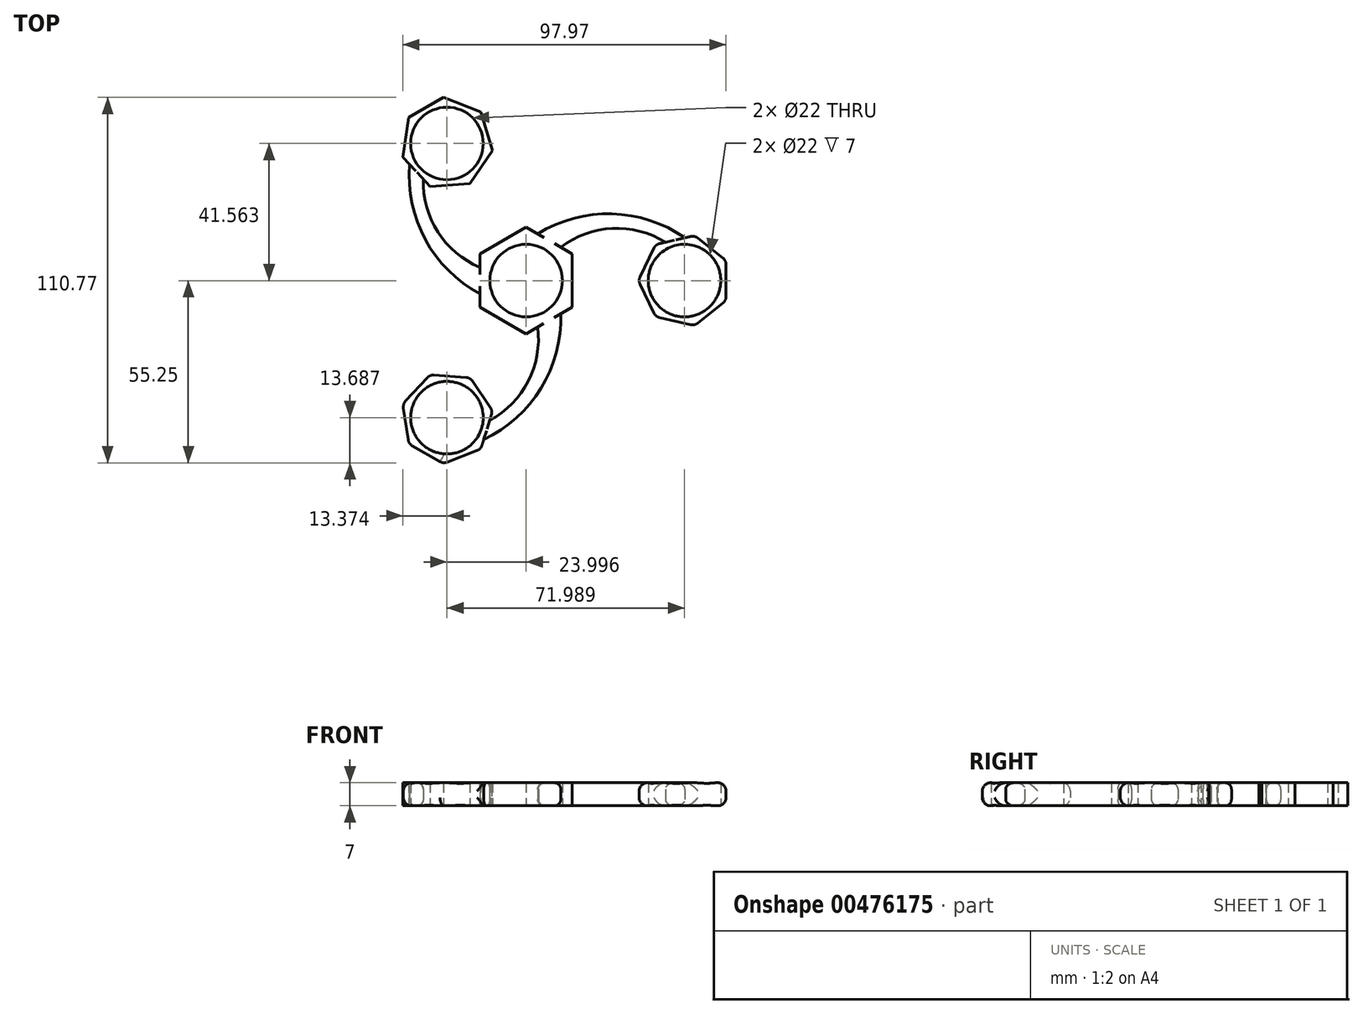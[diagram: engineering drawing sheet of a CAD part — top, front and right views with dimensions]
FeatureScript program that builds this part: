
annotation { "Feature Type Name" : "Feature", "Feature Type Description" : "" }
export const myFeature = defineFeature(function(context is Context, id is Id, definition is map)
    precondition{}
    {
        {
            var Q0;
            Q0=qCreatedBy(makeId("Top.planeOp"),FACE);
            var sketch = newSketch(context, id + "F0", { "sketchPlane" : qUnion([Q0])});
            skCircle(sketch, "E0", {"center": v(0, 0) * mm, "radius": 11 * mm});
            skCircle(sketch, "E1", {"center": v(48, 0) * mm, "radius": 11 * mm});
            skArc(sketch, "E2.cCircle", {"start": v(36.63, 5.47) * mm, "mid": v(50.8, -12.3) * mm, "end": v(55.85, 9.86) * mm, "construction": true});
            skLineSegment(sketch, "E2.0", {"start": v(60.6, 6.07) * mm, "end": v(60.6, -6.07) * mm});
            skLineSegment(sketch, "E2.1", {"start": v(60.6, -6.07) * mm, "end": v(51.1, -13.64) * mm});
            skLineSegment(sketch, "E2.2", {"start": v(51.1, -13.64) * mm, "end": v(39.27, -10.94) * mm});
            skLineSegment(sketch, "E2.3", {"start": v(39.27, -10.94) * mm, "end": v(34, 0) * mm});
            skLineSegment(sketch, "E2.4", {"start": v(34, 0) * mm, "end": v(39.27, 10.94) * mm});
            skLineSegment(sketch, "E2.5", {"start": v(39.27, 10.94) * mm, "end": v(42.23, 11.62) * mm});
            skLineSegment(sketch, "E2.6", {"start": v(51.1, 13.64) * mm, "end": v(60.6, 6.07) * mm});
            skPoint(sketch, "E2.0.midPoint", {"position": v(60.6, 0) * mm});
            skLineSegment(sketch, "E3.0", {"start": v(14, 8.08) * mm, "end": v(14, -8.08) * mm});
            skLineSegment(sketch, "E3.1", {"start": v(14, -8.08) * mm, "end": v(10.5, -10.1) * mm});
            skLineSegment(sketch, "E3.2", {"start": v(0, -16.17) * mm, "end": v(-14, -8.08) * mm});
            skLineSegment(sketch, "E3.3", {"start": v(-14, -8.08) * mm, "end": v(-14, -4.04) * mm});
            skLineSegment(sketch, "E3.4", {"start": v(-14, 8.08) * mm, "end": v(0, 16.17) * mm});
            skLineSegment(sketch, "E3.5", {"start": v(0, 16.17) * mm, "end": v(3.5, 14.15) * mm});
            skPoint(sketch, "E3.0.midPoint", {"position": v(14, 0) * mm});
            skLineSegment(sketch, "E4", {"start": v(14, -8.08) * mm, "end": v(14, 0) * mm});
            skLineSegment(sketch, "E5", {"start": v(14, 0) * mm, "end": v(14, 8.08) * mm});
            skLineSegment(sketch, "E6", {"start": v(14, 8.08) * mm, "end": v(10.5, 10.1) * mm});
            skLineSegment(sketch, "E7", {"start": v(10.5, 10.1) * mm, "end": v(14, 8.08) * mm});
            skLineSegment(sketch, "E8", {"start": v(3.5, 14.15) * mm, "end": v(0, 16.17) * mm});
            skLineSegment(sketch, "E9", {"start": v(48.15, 12.97) * mm, "end": v(51.1, 13.64) * mm});
            skLineSegment(sketch, "E10", {"start": v(42.23, 11.62) * mm, "end": v(39.27, 10.94) * mm});
            skArc(sketch, "E11", {"start": v(42.23, 11.62) * mm, "mid": v(26.13, 15.8) * mm, "end": v(10.5, 10.1) * mm});
            skArc(sketch, "E12", {"start": v(48.15, 12.97) * mm, "mid": v(26, 20.24) * mm, "end": v(3.5, 14.15) * mm});
            skArc(sketch, "E13.1.0", {"start": v(-35.3, 35.21) * mm, "mid": v(-30.53, 12.4) * mm, "end": v(-14, -4.04) * mm});
            skArc(sketch, "E13.1.1", {"start": v(-31.17, 30.76) * mm, "mid": v(-26.75, 14.73) * mm, "end": v(-14, 4.04) * mm});
            skLineSegment(sketch, "E13.1.2", {"start": v(-17, 29.44) * mm, "end": v(-29.1, 28.54) * mm});
            skLineSegment(sketch, "E13.1.3", {"start": v(-10.16, 39.48) * mm, "end": v(-17, 29.44) * mm});
            skLineSegment(sketch, "E13.1.4", {"start": v(-13.74, 51.08) * mm, "end": v(-10.16, 39.48) * mm});
            skLineSegment(sketch, "E13.1.5", {"start": v(-25.04, 55.52) * mm, "end": v(-13.74, 51.08) * mm});
            skLineSegment(sketch, "E13.1.6", {"start": v(-35.56, 49.44) * mm, "end": v(-25.04, 55.52) * mm});
            skLineSegment(sketch, "E13.1.7", {"start": v(-37.37, 37.44) * mm, "end": v(-35.56, 49.44) * mm});
            skLineSegment(sketch, "E13.1.8", {"start": v(-35.3, 35.21) * mm, "end": v(-37.37, 37.44) * mm});
            skLineSegment(sketch, "E13.1.9", {"start": v(-29.1, 28.54) * mm, "end": v(-31.17, 30.76) * mm});
            skCircle(sketch, "E13.1.10", {"center": v(-24, 41.56) * mm, "radius": 11 * mm});
            skArc(sketch, "E13.2.0", {"start": v(-12.84, -48.18) * mm, "mid": v(4.53, -32.64) * mm, "end": v(10.5, -10.1) * mm});
            skArc(sketch, "E13.2.1", {"start": v(-11.05, -42.38) * mm, "mid": v(0.62, -30.53) * mm, "end": v(3.5, -14.15) * mm});
            skLineSegment(sketch, "E13.2.2", {"start": v(-17, -29.44) * mm, "end": v(-10.16, -39.48) * mm});
            skLineSegment(sketch, "E13.2.3", {"start": v(-29.1, -28.54) * mm, "end": v(-17, -29.44) * mm});
            skLineSegment(sketch, "E13.2.4", {"start": v(-37.37, -37.44) * mm, "end": v(-29.1, -28.54) * mm});
            skLineSegment(sketch, "E13.2.5", {"start": v(-35.56, -49.44) * mm, "end": v(-37.37, -37.44) * mm});
            skLineSegment(sketch, "E13.2.6", {"start": v(-25.04, -55.52) * mm, "end": v(-35.56, -49.44) * mm});
            skLineSegment(sketch, "E13.2.7", {"start": v(-13.74, -51.08) * mm, "end": v(-25.04, -55.52) * mm});
            skLineSegment(sketch, "E13.2.8", {"start": v(-12.84, -48.18) * mm, "end": v(-13.74, -51.08) * mm});
            skLineSegment(sketch, "E13.2.9", {"start": v(-10.16, -39.48) * mm, "end": v(-11.05, -42.38) * mm});
            skCircle(sketch, "E13.2.10", {"center": v(-24, -41.56) * mm, "radius": 11 * mm});
            skLineSegment(sketch, "E14.trimOffspring", {"start": v(3.5, -14.15) * mm, "end": v(0, -16.17) * mm});
            skLineSegment(sketch, "E15.trimOffspring", {"start": v(-14, 4.04) * mm, "end": v(-14, 8.08) * mm});
            skSolve(sketch);
        }
        {
            var Q0;
            Q0=makeQuery(id+"F0.imprint","IMPRINT",FACE,{"disambiguationData":[TD([[makeQuery(id+"F0.imprint","IMPRINT",EDGE,{"derivedFrom":sQuery(id+"F0.wireOp",EDGE,"E0")}),-1.0]])]});
            extrude(context, id + "F1", {"entities" : qUnion([Q0]), "depth" : 7 * mm});
        }
        {
            var Q0;
            Q0=makeQuery(id+"F1.opExtrude","CAP_EDGE",EDGE,{"disambiguationData":[OSD([sQuery(id+"F0.wireOp",EDGE,"E13.1.0")])],"isStart":false});
            var Q1;
            Q1=makeQuery(id+"F1.opExtrude","CAP_EDGE",EDGE,{"disambiguationData":[OSD([sQuery(id+"F0.wireOp",EDGE,"E13.2.0")])],"isStart":false});
            var Q2;
            Q2=makeQuery(id+"F1.opExtrude","CAP_EDGE",EDGE,{"disambiguationData":[OSD([sQuery(id+"F0.wireOp",EDGE,"E13.2.1")])],"isStart":false});
            var Q3;
            Q3=makeQuery(id+"F1.opExtrude","CAP_EDGE",EDGE,{"disambiguationData":[OSD([sQuery(id+"F0.wireOp",EDGE,"E11")])],"isStart":false});
            var Q4;
            Q4=makeQuery(id+"F1.opExtrude","CAP_EDGE",EDGE,{"disambiguationData":[OSD([sQuery(id+"F0.wireOp",EDGE,"E12")])],"isStart":false});
            var Q5;
            Q5=makeQuery(id+"F1.opExtrude","CAP_EDGE",EDGE,{"disambiguationData":[OSD([sQuery(id+"F0.wireOp",EDGE,"E13.1.1")])],"isStart":false});
            var Q6;
            Q6=makeQuery(id+"F1.opExtrude","CAP_EDGE",EDGE,{"disambiguationData":[OSD([sQuery(id+"F0.wireOp",EDGE,"E13.2.0")])],"isStart":true});
            var Q7;
            Q7=makeQuery(id+"F1.opExtrude","CAP_EDGE",EDGE,{"disambiguationData":[OSD([sQuery(id+"F0.wireOp",EDGE,"E13.2.1")])],"isStart":true});
            var Q8;
            Q8=makeQuery(id+"F1.opExtrude","CAP_EDGE",EDGE,{"disambiguationData":[OSD([sQuery(id+"F0.wireOp",EDGE,"E11")])],"isStart":true});
            var Q9;
            Q9=makeQuery(id+"F1.opExtrude","CAP_EDGE",EDGE,{"disambiguationData":[OSD([sQuery(id+"F0.wireOp",EDGE,"E12")])],"isStart":true});
            var Q10;
            Q10=makeQuery(id+"F1.opExtrude","CAP_EDGE",EDGE,{"disambiguationData":[OSD([sQuery(id+"F0.wireOp",EDGE,"E13.1.1")])],"isStart":true});
            var Q11;
            Q11=makeQuery(id+"F1.opExtrude","CAP_EDGE",EDGE,{"disambiguationData":[OSD([sQuery(id+"F0.wireOp",EDGE,"E13.1.0")])],"isStart":true});
            fillet(context, id + "F2", {"entities" : qUnion([Q0, Q1, Q2, Q3, Q4, Q5, Q6, Q7, Q8, Q9, Q10, Q11]), "radius" : 2 * mm, "tangentPropagation" : true, "allowEdgeOverflow" : false});
        }
        {
            var Q0;
            Q0=makeQuery(id+"F1.opExtrude","CAP_EDGE",EDGE,{"disambiguationData":[OSD([sQuery(id+"F0.wireOp",EDGE,"E13.2.4")])],"isStart":true});
            var Q1;
            Q1=makeQuery(id+"F1.opExtrude","CAP_EDGE",EDGE,{"disambiguationData":[OSD([sQuery(id+"F0.wireOp",EDGE,"E13.2.5")])],"isStart":true});
            var Q2;
            Q2=makeQuery(id+"F1.opExtrude","CAP_EDGE",EDGE,{"disambiguationData":[OSD([sQuery(id+"F0.wireOp",EDGE,"E13.2.6")])],"isStart":true});
            var Q3;
            Q3=makeQuery(id+"F1.opExtrude","CAP_EDGE",EDGE,{"disambiguationData":[OSD([sQuery(id+"F0.wireOp",EDGE,"E13.2.3")])],"isStart":true});
            var Q4;
            Q4=makeQuery(id+"F1.opExtrude","CAP_EDGE",EDGE,{"disambiguationData":[OSD([sQuery(id+"F0.wireOp",EDGE,"E13.2.2")])],"isStart":true});
            var Q5;
            Q5=makeQuery(id+"F1.opExtrude","CAP_EDGE",EDGE,{"disambiguationData":[OSD([sQuery(id+"F0.wireOp",EDGE,"E13.2.7")])],"isStart":true});
            var Q6;
            Q6=makeQuery(id+"F1.opExtrude","CAP_EDGE",EDGE,{"disambiguationData":[OSD([sQuery(id+"F0.wireOp",EDGE,"E13.2.6")])],"isStart":false});
            var Q7;
            Q7=makeQuery(id+"F1.opExtrude","CAP_EDGE",EDGE,{"disambiguationData":[OSD([sQuery(id+"F0.wireOp",EDGE,"E13.2.7")])],"isStart":false});
            var Q8;
            Q8=makeQuery(id+"F1.opExtrude","CAP_EDGE",EDGE,{"disambiguationData":[OSD([sQuery(id+"F0.wireOp",EDGE,"E13.2.2")])],"isStart":false});
            var Q9;
            Q9=makeQuery(id+"F1.opExtrude","CAP_EDGE",EDGE,{"disambiguationData":[OSD([sQuery(id+"F0.wireOp",EDGE,"E13.2.3")])],"isStart":false});
            var Q10;
            Q10=makeQuery(id+"F1.opExtrude","CAP_EDGE",EDGE,{"disambiguationData":[OSD([sQuery(id+"F0.wireOp",EDGE,"E13.2.4")])],"isStart":false});
            var Q11;
            Q11=makeQuery(id+"F1.opExtrude","CAP_EDGE",EDGE,{"disambiguationData":[OSD([sQuery(id+"F0.wireOp",EDGE,"E13.2.5")])],"isStart":false});
            var Q12;
            Q12=makeQuery(id+"F1.opExtrude","SWEPT_EDGE",EDGE,{"disambiguationData":[OSD([sQuery(id+"F0.wireOp",EDGE,"E13.2.4"),sQuery(id+"F0.wireOp",EDGE,"E13.2.5")])]});
            var Q13;
            Q13=makeQuery(id+"F1.opExtrude","SWEPT_EDGE",EDGE,{"disambiguationData":[OSD([sQuery(id+"F0.wireOp",EDGE,"E13.2.5"),sQuery(id+"F0.wireOp",EDGE,"E13.2.6")])]});
            var Q14;
            Q14=makeQuery(id+"F1.opExtrude","SWEPT_EDGE",EDGE,{"disambiguationData":[OSD([sQuery(id+"F0.wireOp",EDGE,"E13.2.6"),sQuery(id+"F0.wireOp",EDGE,"E13.2.7")])]});
            var Q15;
            Q15=makeQuery(id+"F1.opExtrude","SWEPT_FACE",FACE,{"disambiguationData":[OSD([sQuery(id+"F0.wireOp",EDGE,"E13.2.4")])]});
            var Q16;
            Q16=makeQuery(id+"F1.opExtrude","SWEPT_FACE",FACE,{"disambiguationData":[OSD([sQuery(id+"F0.wireOp",EDGE,"E13.2.3")])]});
            var Q17;
            Q17=makeQuery(id+"F1.opExtrude","SWEPT_FACE",FACE,{"disambiguationData":[OSD([sQuery(id+"F0.wireOp",EDGE,"E13.2.2")])]});
            var Q18;
            Q18=makeQuery(id+"F1.opExtrude","SWEPT_FACE",FACE,{"disambiguationData":[OSD([sQuery(id+"F0.wireOp",EDGE,"E13.2.7")])]});
            var Q19;
            Q19=makeQuery(id+"F1.opExtrude","SWEPT_FACE",FACE,{"disambiguationData":[OSD([sQuery(id+"F0.wireOp",EDGE,"E2.6")])]});
            var Q20;
            Q20=makeQuery(id+"F1.opExtrude","SWEPT_FACE",FACE,{"disambiguationData":[OSD([sQuery(id+"F0.wireOp",EDGE,"E2.0")])]});
            var Q21;
            Q21=makeQuery(id+"F1.opExtrude","SWEPT_FACE",FACE,{"disambiguationData":[OSD([sQuery(id+"F0.wireOp",EDGE,"E2.1")])]});
            var Q22;
            Q22=makeQuery(id+"F1.opExtrude","SWEPT_FACE",FACE,{"disambiguationData":[OSD([sQuery(id+"F0.wireOp",EDGE,"E2.2")])]});
            var Q23;
            Q23=makeQuery(id+"F1.opExtrude","SWEPT_FACE",FACE,{"disambiguationData":[OSD([sQuery(id+"F0.wireOp",EDGE,"E2.4")])]});
            var Q24;
            Q24=makeQuery(id+"F1.opExtrude","SWEPT_FACE",FACE,{"disambiguationData":[OSD([sQuery(id+"F0.wireOp",EDGE,"E2.3")])]});
            fillet(context, id + "F3", {"entities" : qUnion([Q0, Q1, Q2, Q3, Q4, Q5, Q6, Q7, Q8, Q9, Q10, Q11, Q12, Q13, Q14, Q15, Q16, Q17, Q18, Q19, Q20, Q21, Q22, Q23, Q24]), "radius" : 2.5 * mm, "tangentPropagation" : true, "allowEdgeOverflow" : false});
        }
    });
